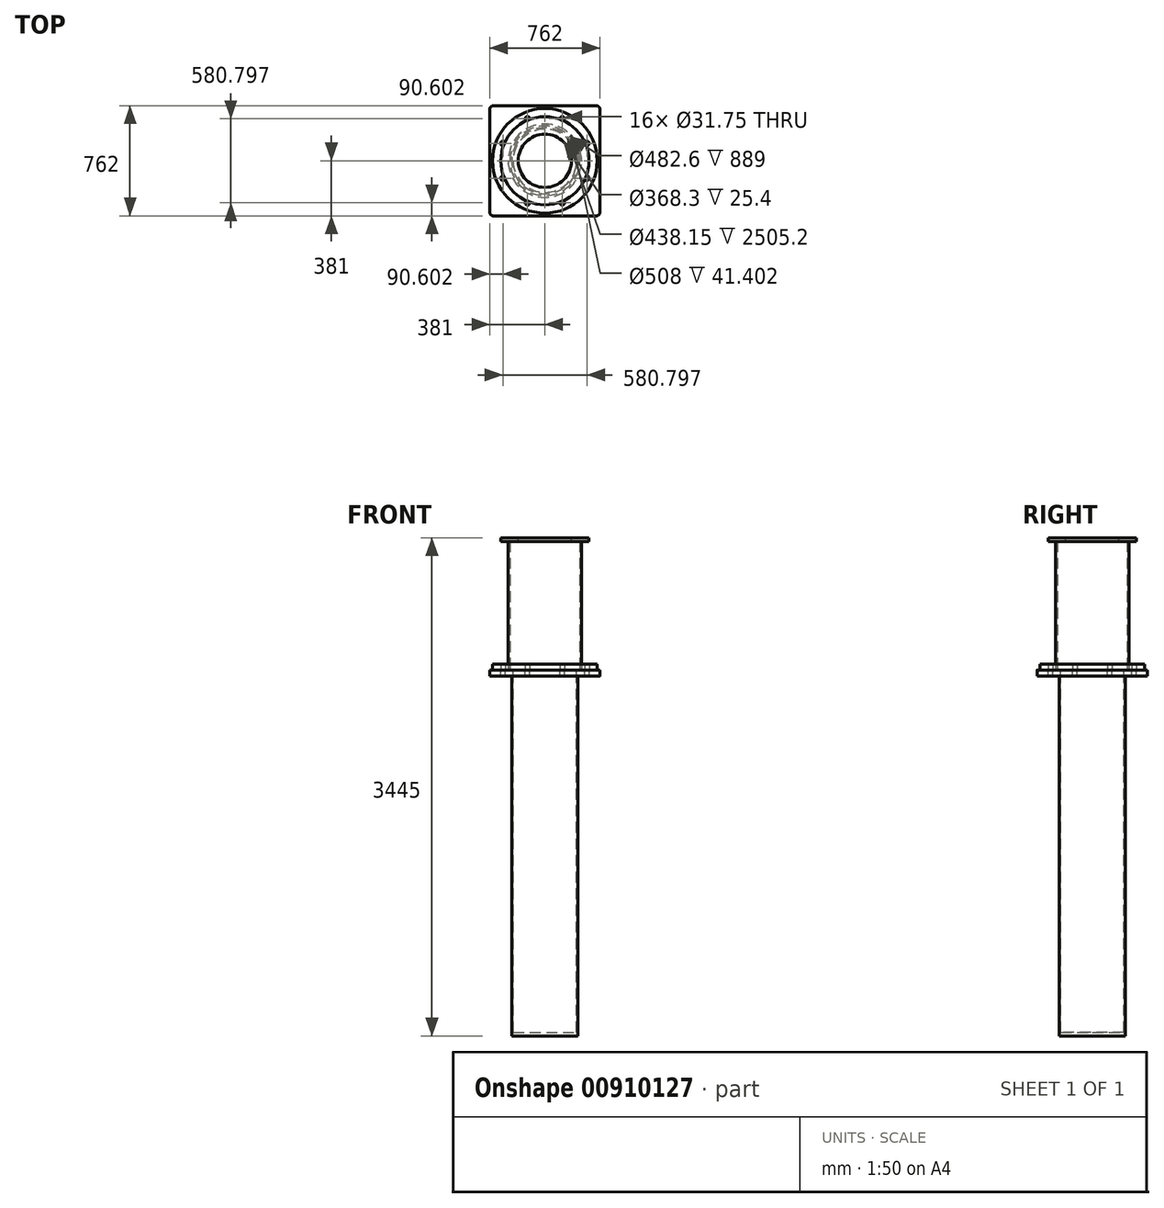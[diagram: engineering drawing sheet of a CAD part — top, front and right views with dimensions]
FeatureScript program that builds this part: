
annotation { "Feature Type Name" : "Feature", "Feature Type Description" : "" }
export const myFeature = defineFeature(function(context is Context, id is Id, definition is map)
    precondition{}
    {
        {
            var Q0;
            Q0=qCreatedBy(makeId("Top.planeOp"),FACE);
            var sketch = newSketch(context, id + "F0", { "sketchPlane" : qUnion([Q0])});
            skCircle(sketch, "E0", {"center": v(0, 0) * mm, "radius": 228.6 * mm});
            skCircle(sketch, "E1", {"center": v(0, 0) * mm, "radius": 314.33 * mm, "construction": true});
            skLineSegment(sketch, "E2.bottom", {"start": v(381, 381) * mm, "end": v(-381, 381) * mm});
            skLineSegment(sketch, "E2.top", {"start": v(381, -381) * mm, "end": v(-381, -381) * mm});
            skLineSegment(sketch, "E2.left", {"start": v(381, 381) * mm, "end": v(381, -381) * mm});
            skLineSegment(sketch, "E2.right", {"start": v(-381, 381) * mm, "end": v(-381, -381) * mm});
            skLineSegment(sketch, "E3", {"start": v(0, 0) * mm, "end": v(0, 539.8) * mm, "construction": true});
            skLineSegment(sketch, "E4", {"start": v(0, 0) * mm, "end": v(212.56, 513.15) * mm, "construction": true});
            skCircle(sketch, "E5", {"center": v(120.29, 290.4) * mm, "radius": 15.88 * mm});
            skCircle(sketch, "E6.1.0", {"center": v(-120.29, 290.4) * mm, "radius": 15.88 * mm});
            skCircle(sketch, "E6.2.0", {"center": v(-290.4, 120.29) * mm, "radius": 15.88 * mm});
            skCircle(sketch, "E6.3.0", {"center": v(-290.4, -120.29) * mm, "radius": 15.88 * mm});
            skCircle(sketch, "E6.4.0", {"center": v(-120.29, -290.4) * mm, "radius": 15.88 * mm});
            skCircle(sketch, "E6.5.0", {"center": v(120.29, -290.4) * mm, "radius": 15.88 * mm});
            skCircle(sketch, "E6.6.0", {"center": v(290.4, -120.29) * mm, "radius": 15.88 * mm});
            skCircle(sketch, "E6.7.0", {"center": v(290.4, 120.29) * mm, "radius": 15.88 * mm});
            skSolve(sketch);
        }
        {
            var Q0;
            Q0 = qSketchRegion(id + "F0", true);
            extrude(context, id + "F1", {"entities" : qUnion([Q0]), "oppositeDirection" : true, "depth" : 41.4 * mm, "offsetDistance" : 25.4 * mm});
        }
        {
            var Q0;
            Q0=makeQuery(id+"F1.opExtrude","CAP_FACE",FACE,{"disambiguationData":[OSD([sQuery(id+"F0.wireOp",EDGE,"E0"),sQuery(id+"F0.wireOp",EDGE,"E2.bottom"),sQuery(id+"F0.wireOp",EDGE,"E2.top"),sQuery(id+"F0.wireOp",EDGE,"E2.left"),sQuery(id+"F0.wireOp",EDGE,"E2.right"),sQuery(id+"F0.wireOp",EDGE,"E5"),sQuery(id+"F0.wireOp",EDGE,"E6.1.0"),sQuery(id+"F0.wireOp",EDGE,"E6.2.0"),sQuery(id+"F0.wireOp",EDGE,"E6.3.0"),sQuery(id+"F0.wireOp",EDGE,"E6.4.0"),sQuery(id+"F0.wireOp",EDGE,"E6.5.0"),sQuery(id+"F0.wireOp",EDGE,"E6.6.0"),sQuery(id+"F0.wireOp",EDGE,"E6.7.0")])],"isStart":false});
            var sketch = newSketch(context, id + "F2", { "sketchPlane" : qUnion([Q0])});
            skCircle(sketch, "E7", {"center": v(0, 0) * mm, "radius": 228.6 * mm});
            skCircle(sketch, "E8", {"center": v(0, 0) * mm, "radius": 219.08 * mm});
            skSolve(sketch);
        }
        {
            var Q0;
            Q0 = qSketchRegion(id + "F2", true);
            extrude(context, id + "F3", {"entities" : qUnion([Q0]), "operationType" : NewBodyOperationType.ADD, "depth" : 2489.2 * mm, "offsetDistance" : 25.4 * mm, "hasSecondDirection" : true, "secondDirectionOppositeDirection" : true, "secondDirectionDepth" : 41.4 * mm});
        }
        {
            var Q0;
            Q0=makeQuery(id+"F3.opExtrude","CAP_FACE",FACE,{"disambiguationData":[OSD([sQuery(id+"F2.wireOp",EDGE,"E7"),sQuery(id+"F2.wireOp",EDGE,"E8")])],"isStart":false});
            var sketch = newSketch(context, id + "F4", { "sketchPlane" : qUnion([Q0])});
            skCircle(sketch, "E9", {"center": v(0, 0) * mm, "radius": 228.6 * mm});
            skSolve(sketch);
        }
        {
            var Q0;
            Q0 = qSketchRegion(id + "F4", true);
            extrude(context, id + "F5", {"entities" : qUnion([Q0]), "operationType" : NewBodyOperationType.ADD, "oppositeDirection" : true, "depth" : 25.4 * mm, "offsetDistance" : 25.4 * mm});
        }
        {
            var Q0;
            Q0=makeQuery(id+"F1.opExtrude","SWEPT_EDGE",EDGE,{"disambiguationData":[OSD([sQuery(id+"F0.wireOp",EDGE,"E2.top"),sQuery(id+"F0.wireOp",EDGE,"E2.left")])]});
            var Q1;
            Q1=makeQuery(id+"F1.opExtrude","SWEPT_EDGE",EDGE,{"disambiguationData":[OSD([sQuery(id+"F0.wireOp",EDGE,"E2.bottom"),sQuery(id+"F0.wireOp",EDGE,"E2.left")])]});
            var Q2;
            Q2=makeQuery(id+"F1.opExtrude","SWEPT_EDGE",EDGE,{"disambiguationData":[OSD([sQuery(id+"F0.wireOp",EDGE,"E2.top"),sQuery(id+"F0.wireOp",EDGE,"E2.right")])]});
            var Q3;
            Q3=makeQuery(id+"F1.opExtrude","SWEPT_EDGE",EDGE,{"disambiguationData":[OSD([sQuery(id+"F0.wireOp",EDGE,"E2.bottom"),sQuery(id+"F0.wireOp",EDGE,"E2.right")])]});
            fillet(context, id + "F6", {"entities" : qUnion([Q0, Q1, Q2, Q3]), "radius" : 25.4 * mm, "tangentPropagation" : true, "allowEdgeOverflow" : false});
        }
        {
            var Q0;
            Q0=makeQuery(id+"F3.boolean.opBoolean","MERGE",FACE,{"derivedFrom":[makeQuery(id+"F1.opExtrude","CAP_FACE",FACE,{"disambiguationData":[OSD([sQuery(id+"F0.wireOp",EDGE,"E0"),sQuery(id+"F0.wireOp",EDGE,"E2.bottom"),sQuery(id+"F0.wireOp",EDGE,"E2.top"),sQuery(id+"F0.wireOp",EDGE,"E2.left"),sQuery(id+"F0.wireOp",EDGE,"E2.right"),sQuery(id+"F0.wireOp",EDGE,"E5"),sQuery(id+"F0.wireOp",EDGE,"E6.1.0"),sQuery(id+"F0.wireOp",EDGE,"E6.2.0"),sQuery(id+"F0.wireOp",EDGE,"E6.3.0"),sQuery(id+"F0.wireOp",EDGE,"E6.4.0"),sQuery(id+"F0.wireOp",EDGE,"E6.5.0"),sQuery(id+"F0.wireOp",EDGE,"E6.6.0"),sQuery(id+"F0.wireOp",EDGE,"E6.7.0")])],"isStart":true}),makeQuery(id+"F3.opExtrude","CAP_FACE",FACE,{"disambiguationData":[OSD([sQuery(id+"F2.wireOp",EDGE,"E7"),sQuery(id+"F2.wireOp",EDGE,"E8")])],"isStart":true})]});
            var sketch = newSketch(context, id + "F7", { "sketchPlane" : qUnion([Q0])});
            skCircle(sketch, "E10", {"center": v(0, 0) * mm, "radius": 361.95 * mm});
            skCircle(sketch, "E11", {"center": v(0, 0) * mm, "radius": 254 * mm});
            skCircle(sketch, "E12", {"center": v(0, 0) * mm, "radius": 314.33 * mm, "construction": true});
            skLineSegment(sketch, "E13", {"start": v(0, 0) * mm, "end": v(0, 546.23) * mm, "construction": true});
            skLineSegment(sketch, "E14", {"start": v(0, 0) * mm, "end": v(191.06, 461.25) * mm, "construction": true});
            skCircle(sketch, "E15", {"center": v(120.29, 290.4) * mm, "radius": 15.88 * mm});
            skCircle(sketch, "E16.1.0", {"center": v(-120.29, 290.4) * mm, "radius": 15.88 * mm});
            skCircle(sketch, "E16.2.0", {"center": v(-290.4, 120.29) * mm, "radius": 15.88 * mm});
            skCircle(sketch, "E16.3.0", {"center": v(-290.4, -120.29) * mm, "radius": 15.88 * mm});
            skCircle(sketch, "E16.4.0", {"center": v(-120.29, -290.4) * mm, "radius": 15.88 * mm});
            skCircle(sketch, "E16.5.0", {"center": v(120.29, -290.4) * mm, "radius": 15.88 * mm});
            skCircle(sketch, "E16.6.0", {"center": v(290.4, -120.29) * mm, "radius": 15.88 * mm});
            skCircle(sketch, "E16.7.0", {"center": v(290.4, 120.29) * mm, "radius": 15.88 * mm});
            skSolve(sketch);
        }
        {
            var Q0;
            Q0 = qSketchRegion(id + "F7", true);
            extrude(context, id + "F8", {"entities" : qUnion([Q0]), "depth" : 41.4 * mm, "offsetDistance" : 25.4 * mm});
        }
        {
            var Q0;
            Q0=makeQuery(id+"F3.boolean.opBoolean","MERGE",FACE,{"derivedFrom":[makeQuery(id+"F1.opExtrude","CAP_FACE",FACE,{"disambiguationData":[OSD([sQuery(id+"F0.wireOp",EDGE,"E0"),sQuery(id+"F0.wireOp",EDGE,"E2.bottom"),sQuery(id+"F0.wireOp",EDGE,"E2.top"),sQuery(id+"F0.wireOp",EDGE,"E2.left"),sQuery(id+"F0.wireOp",EDGE,"E2.right"),sQuery(id+"F0.wireOp",EDGE,"E5"),sQuery(id+"F0.wireOp",EDGE,"E6.1.0"),sQuery(id+"F0.wireOp",EDGE,"E6.2.0"),sQuery(id+"F0.wireOp",EDGE,"E6.3.0"),sQuery(id+"F0.wireOp",EDGE,"E6.4.0"),sQuery(id+"F0.wireOp",EDGE,"E6.5.0"),sQuery(id+"F0.wireOp",EDGE,"E6.6.0"),sQuery(id+"F0.wireOp",EDGE,"E6.7.0")])],"isStart":true}),makeQuery(id+"F3.opExtrude","CAP_FACE",FACE,{"disambiguationData":[OSD([sQuery(id+"F2.wireOp",EDGE,"E7"),sQuery(id+"F2.wireOp",EDGE,"E8")])],"isStart":true})]});
            var sketch = newSketch(context, id + "F9", { "sketchPlane" : qUnion([Q0])});
            skCircle(sketch, "E17", {"center": v(0, 0) * mm, "radius": 254 * mm});
            skCircle(sketch, "E18", {"center": v(0, 0) * mm, "radius": 241.3 * mm});
            skSolve(sketch);
        }
        {
            var Q0;
            Q0 = qSketchRegion(id + "F9", true);
            extrude(context, id + "F10", {"entities" : qUnion([Q0]), "depth" : 914.4 * mm, "offsetDistance" : 25.4 * mm});
        }
        {
            var Q0;
            Q0=makeQuery(id+"F10.opExtrude","CAP_FACE",FACE,{"disambiguationData":[OSD([sQuery(id+"F9.wireOp",EDGE,"E17"),sQuery(id+"F9.wireOp",EDGE,"E18")])],"isStart":false});
            var sketch = newSketch(context, id + "F11", { "sketchPlane" : qUnion([Q0])});
            skCircle(sketch, "E19", {"center": v(0, 0) * mm, "radius": 184.15 * mm});
            skCircle(sketch, "E20", {"center": v(0, 0) * mm, "radius": 304.8 * mm});
            skSolve(sketch);
        }
        {
            var Q0;
            Q0 = qSketchRegion(id + "F11", true);
            extrude(context, id + "F12", {"entities" : qUnion([Q0]), "operationType" : NewBodyOperationType.ADD, "oppositeDirection" : true, "depth" : 25.4 * mm, "offsetDistance" : 25.4 * mm});
        }
    });
